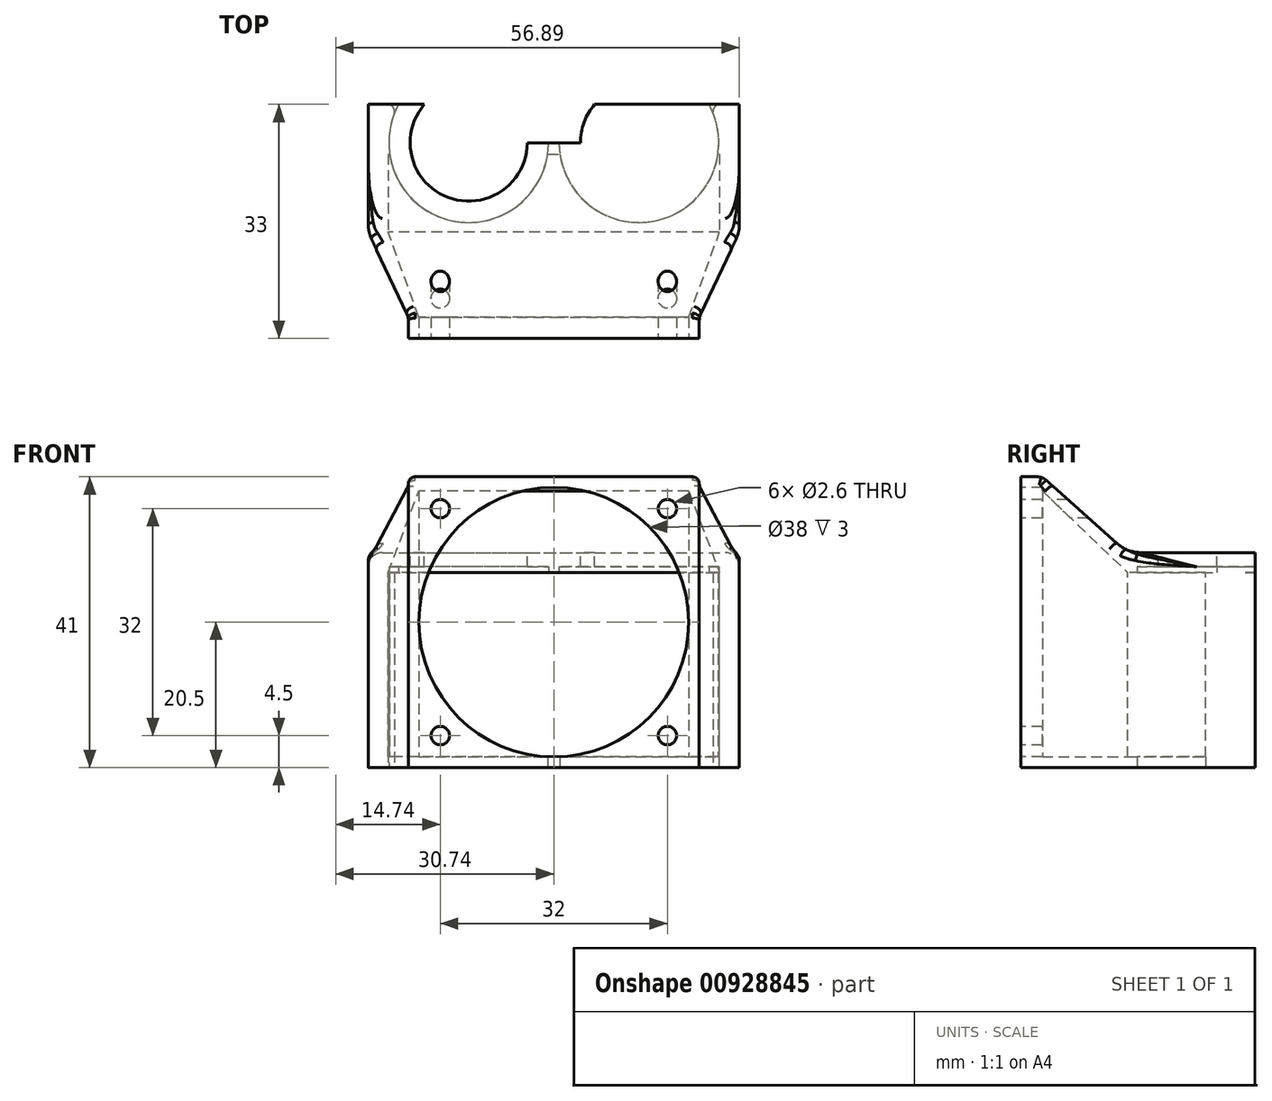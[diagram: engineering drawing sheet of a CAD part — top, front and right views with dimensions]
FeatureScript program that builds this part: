
annotation { "Feature Type Name" : "Feature", "Feature Type Description" : "" }
export const myFeature = defineFeature(function(context is Context, id is Id, definition is map)
    precondition{}
    {
        {
            var Q0;
            Q0=qCreatedBy(makeId("Front.planeOp"),FACE);
            var sketch = newSketch(context, id + "F0", { "sketchPlane" : qUnion([Q0])});
            skLineSegment(sketch, "E0.bottom", {"start": v(23.35, -13.75) * mm, "end": v(-23.35, -13.75) * mm});
            skLineSegment(sketch, "E0.top", {"start": v(23.35, 13.75) * mm, "end": v(-23.35, 13.75) * mm});
            skLineSegment(sketch, "E0.left", {"start": v(23.35, -13.75) * mm, "end": v(23.35, 13.75) * mm});
            skLineSegment(sketch, "E0.right", {"start": v(-23.35, -13.75) * mm, "end": v(-23.35, 13.75) * mm});
            skPoint(sketch, "E0.middle", {"position": v(0, 0) * mm});
            skLineSegment(sketch, "E1.bottom", {"start": v(-26.15, 16.55) * mm, "end": v(26.15, 16.55) * mm});
            skLineSegment(sketch, "E1.top", {"start": v(-26.15, -13.75) * mm, "end": v(26.15, -13.75) * mm});
            skLineSegment(sketch, "E1.left", {"start": v(-26.15, 16.55) * mm, "end": v(-26.15, -13.75) * mm});
            skLineSegment(sketch, "E1.right", {"start": v(26.15, 16.55) * mm, "end": v(26.15, -13.75) * mm});
            skLineSegment(sketch, "E2", {"start": v(-23.35, 13.75) * mm, "end": v(-26.15, 16.55) * mm});
            skLineSegment(sketch, "E3", {"start": v(23.35, 13.75) * mm, "end": v(26.15, 16.55) * mm});
            skSolve(sketch);
        }
        {
            var Q0;
            Q0=makeQuery(id+"F0.imprint","IMPRINT",FACE,{"disambiguationData":[TD([[makeQuery(id+"F0.imprint","IMPRINT",EDGE,{"derivedFrom":sQuery(id+"F0.wireOp",EDGE,"E0.top")}),-1.0]])]});
            var Q1;
            {var subQ0=sQuery(id+"F0.wireOp",EDGE,"E0.left");Q1=makeQuery(id+"F0.imprint","IMPRINT",FACE,{"disambiguationData":[TD([[makeQuery(id+"F0.imprint","IMPRINT",EDGE,{"derivedFrom":subQ0}),-1.0]])]});}
            var Q2;
            {var subQ0=sQuery(id+"F0.wireOp",EDGE,"E0.right");Q2=makeQuery(id+"F0.imprint","IMPRINT",FACE,{"disambiguationData":[TD([[makeQuery(id+"F0.imprint","IMPRINT",EDGE,{"derivedFrom":subQ0}),1.0]])]});}
            extrude(context, id + "F1", {"entities" : qUnion([Q0, Q1, Q2]), "oppositeDirection" : true, "depth" : 18 * mm, "offsetDistance" : 25 * mm});
        }
        {
            var Q0;
            Q0=makeQuery(id+"F1.opExtrude","SWEPT_FACE",FACE,{"disambiguationData":[OSD([sQuery(id+"F0.wireOp",EDGE,"E1.bottom")])]});
            var sketch = newSketch(context, id + "F2", { "sketchPlane" : qUnion([Q0])});
            skCircle(sketch, "E4", {"center": v(-12, 12.6) * mm, "radius": 8.25 * mm});
            skCircle(sketch, "E5.MirrorC", {"center": v(12, 12.6) * mm, "radius": 8.25 * mm});
            skLineSegment(sketch, "E6", {"start": v(-3.75, 12.6) * mm, "end": v(3.75, 12.6) * mm});
            skSolve(sketch);
        }
        {
            var Q0;
            Q0=makeQuery(id+"F2.imprint","IMPRINT",FACE,{"disambiguationData":[TD([[makeQuery(id+"F2.imprint","IMPRINT",EDGE,{"derivedFrom":sQuery(id+"F2.wireOp",EDGE,"E4")}),1.0]])]});
            var Q1;
            Q1=makeQuery(id+"F2.imprint","IMPRINT",FACE,{"disambiguationData":[TD([[makeQuery(id+"F2.imprint","IMPRINT",EDGE,{"derivedFrom":sQuery(id+"F2.wireOp",EDGE,"E5.MirrorC")}),-1.0]])]});
            var Q2;
            {var subQ0=sQuery(id+"F2.wireOp",EDGE,"E6");Q2=makeQuery(id+"F2.imprint","IMPRINT",FACE,{"disambiguationData":[TD([[makeQuery(id+"F2.imprint","IMPRINT",EDGE,{"derivedFrom":subQ0}),1.0]])]});}
            extrude(context, id + "F3", {"entities" : qUnion([Q0, Q1, Q2]), "operationType" : NewBodyOperationType.REMOVE, "oppositeDirection" : true, "depth" : 25 * mm, "offsetDistance" : 25 * mm});
        }
        {
            var Q0;
            Q0=qCreatedBy(makeId("Front.planeOp"),FACE);
            cPlane(context, id + "F4", {"entities" : qUnion([Q0]), "cplaneType" : CPlaneType.OFFSET, "offset" : 15 * mm, "width" : 150 * mm, "height" : 150 * mm});
        }
        {
            var Q0;
            Q0=qCreatedBy(id+"F4.planeOp",FACE);
            var sketch = newSketch(context, id + "F5", { "sketchPlane" : qUnion([Q0])});
            skLineSegment(sketch, "E7.bottom", {"start": v(-26.15, -13.75) * mm, "end": v(26.15, -13.75) * mm, "construction": true});
            skLineSegment(sketch, "E7.top", {"start": v(-26.15, 16.55) * mm, "end": v(26.15, 16.55) * mm, "construction": true});
            skLineSegment(sketch, "E7.left", {"start": v(-26.15, -13.75) * mm, "end": v(-26.15, 16.55) * mm, "construction": true});
            skLineSegment(sketch, "E7.right", {"start": v(26.15, -13.75) * mm, "end": v(26.15, 16.55) * mm, "construction": true});
            skLineSegment(sketch, "E8.bottom", {"start": v(-20.5, -13.75) * mm, "end": v(20.5, -13.75) * mm});
            skLineSegment(sketch, "E8.top", {"start": v(-20.5, 27.25) * mm, "end": v(20.5, 27.25) * mm});
            skLineSegment(sketch, "E8.left", {"start": v(-20.5, -13.75) * mm, "end": v(-20.5, 27.25) * mm});
            skLineSegment(sketch, "E8.right", {"start": v(20.5, -13.75) * mm, "end": v(20.5, 27.25) * mm});
            skPoint(sketch, "E9.centerSnap0", {"position": v(-20.5, 6.75) * mm});
            skSolve(sketch);
        }
        {
            var Q0;
            Q0=makeQuery(id+"F5.imprint","IMPRINT",FACE,{"disambiguationData":[TD([[makeQuery(id+"F5.imprint","IMPRINT",EDGE,{"derivedFrom":sQuery(id+"F5.wireOp",EDGE,"E8.bottom")}),1.0]])]});
            extrude(context, id + "F6", {"entities" : qUnion([Q0]), "oppositeDirection" : true, "depth" : 3 * mm, "offsetDistance" : 25 * mm});
        }
        {
            var Q0;
            Q0=makeQuery(id+"F6.opExtrude","CAP_FACE",FACE,{"disambiguationData":[OSD([sQuery(id+"F5.wireOp",EDGE,"E8.bottom"),sQuery(id+"F5.wireOp",EDGE,"E8.top"),sQuery(id+"F5.wireOp",EDGE,"E8.left"),sQuery(id+"F5.wireOp",EDGE,"E8.right")])],"isStart":false});
            var sketch = newSketch(context, id + "F7", { "sketchPlane" : qUnion([Q0])});
            skLineSegment(sketch, "E10.bottom", {"start": v(-19, 25.25) * mm, "end": v(19, 25.25) * mm});
            skLineSegment(sketch, "E10.top", {"start": v(-19, -13.75) * mm, "end": v(19, -13.75) * mm});
            skLineSegment(sketch, "E10.left", {"start": v(-19, 25.25) * mm, "end": v(-19, -13.75) * mm});
            skLineSegment(sketch, "E10.right", {"start": v(19, 25.25) * mm, "end": v(19, -13.75) * mm});
            skLineSegment(sketch, "E11", {"start": v(-19, 25.25) * mm, "end": v(-20.5, 27.25) * mm});
            skLineSegment(sketch, "E12", {"start": v(20.5, 27.25) * mm, "end": v(19, 25.25) * mm});
            skSolve(sketch);
        }
        {
            var Q0;
            {var subQ0=sQuery(id+"F7.wireOp",EDGE,"E10.left");Q0=makeQuery(id+"F7.imprint","IMPRINT",FACE,{"disambiguationData":[TD([[makeQuery(id+"F7.imprint","IMPRINT",EDGE,{"derivedFrom":subQ0}),-1.0]])]});}
            var Q1;
            {var subQ0=sQuery(id+"F0.wireOp",EDGE,"E0.left");Q1=makeQuery(id+"F0.imprint","IMPRINT",FACE,{"disambiguationData":[TD([[makeQuery(id+"F0.imprint","IMPRINT",EDGE,{"derivedFrom":subQ0}),-1.0]])]});}
            loft(context, id + "F8", {"operationType" : NewBodyOperationType.ADD, "sheetProfilesArray" : [{ "sheetProfileEntities" : qUnion([Q0]) }, { "sheetProfileEntities" : qUnion([Q1]) }]});
        }
        {
            var Q1;
            {var subQ0=sQuery(id+"F0.wireOp",EDGE,"E0.right");Q1=makeQuery(id+"F0.imprint","IMPRINT",FACE,{"disambiguationData":[TD([[makeQuery(id+"F0.imprint","IMPRINT",EDGE,{"derivedFrom":subQ0}),1.0]])]});}
            var Q2;
            {var subQ0=sQuery(id+"F7.wireOp",EDGE,"E10.right");Q2=makeQuery(id+"F7.imprint","IMPRINT",FACE,{"disambiguationData":[TD([[makeQuery(id+"F7.imprint","IMPRINT",EDGE,{"derivedFrom":subQ0}),1.0]])]});}
            loft(context, id + "F9", {"operationType" : NewBodyOperationType.ADD, "sheetProfilesArray" : [{ "sheetProfileEntities" : qUnion([Q1]) }, { "sheetProfileEntities" : qUnion([Q2]) }]});
        }
        {
            var Q1;
            Q1=makeQuery(id+"F7.imprint","IMPRINT",FACE,{"disambiguationData":[TD([[makeQuery(id+"F7.imprint","IMPRINT",EDGE,{"derivedFrom":sQuery(id+"F7.wireOp",EDGE,"E10.bottom")}),1.0]])]});
            var Q2;
            Q2=makeQuery(id+"F0.imprint","IMPRINT",FACE,{"disambiguationData":[TD([[makeQuery(id+"F0.imprint","IMPRINT",EDGE,{"derivedFrom":sQuery(id+"F0.wireOp",EDGE,"E0.top")}),-1.0]])]});
            loft(context, id + "F10", {"operationType" : NewBodyOperationType.ADD, "sheetProfilesArray" : [{ "sheetProfileEntities" : qUnion([Q1]) }, { "sheetProfileEntities" : qUnion([Q2]) }]});
        }
        {
            var Q0;
            Q0=makeQuery(id+"F6.opExtrude","CAP_FACE",FACE,{"disambiguationData":[OSD([sQuery(id+"F5.wireOp",EDGE,"E8.bottom"),sQuery(id+"F5.wireOp",EDGE,"E8.top"),sQuery(id+"F5.wireOp",EDGE,"E8.left"),sQuery(id+"F5.wireOp",EDGE,"E8.right")])],"isStart":true});
            var sketch = newSketch(context, id + "F11", { "sketchPlane" : qUnion([Q0])});
            skCircle(sketch, "E13", {"center": v(0, 6.75) * mm, "radius": 19 * mm});
            skLineSegment(sketch, "E14", {"start": v(-20.5, 6.75) * mm, "end": v(20.5, 6.75) * mm, "construction": true});
            skLineSegment(sketch, "E15", {"start": v(0, 27.25) * mm, "end": v(0, -13.75) * mm, "construction": true});
            skPoint(sketch, "E16", {"position": v(-16, 22.75) * mm});
            skPoint(sketch, "E17.MirrorP", {"position": v(16, 22.75) * mm});
            skPoint(sketch, "E18.MirrorP", {"position": v(-16, -9.25) * mm});
            skPoint(sketch, "E19.MirrorP", {"position": v(16, -9.25) * mm});
            skSolve(sketch);
        }
        {
            var Q0;
            Q0=sQuery(id+"F11.wireOp",VERTEX,"E16");
            var Q1;
            Q1=sQuery(id+"F11.wireOp",VERTEX,"E17.MirrorP");
            var Q2;
            Q2=sQuery(id+"F11.wireOp",VERTEX,"E19.MirrorP");
            var Q3;
            Q3=sQuery(id+"F11.wireOp",VERTEX,"E18.MirrorP");
            var Q4;
            Q4=makeQuery(id+"F1.opExtrude","SWEPT_BODY",BODY,{"disambiguationData":[OSD([sQuery(id+"F0.wireOp",EDGE,"E0.top"),sQuery(id+"F0.wireOp",EDGE,"E0.left"),sQuery(id+"F0.wireOp",EDGE,"E0.right"),sQuery(id+"F0.wireOp",EDGE,"E1.bottom"),sQuery(id+"F0.wireOp",EDGE,"E1.top"),sQuery(id+"F0.wireOp",EDGE,"E1.left"),sQuery(id+"F0.wireOp",EDGE,"E1.right")])]});
            hole(context, id + "F12", {"style" : HoleStyle.SIMPLE, "endStyle" : HoleEndStyle.BLIND, "holeDiameter" : 2.6 * mm, "majorDiameter" : 5 * mm, "holeDepth" : 10 * mm, "isTappedThrough" : true, "tappedDepth" : 12 * mm, "tapClearance" : 3, "locations" : qUnion([Q0, Q1, Q2, Q3]), "scope" : qUnion([Q4])});
        }
        {
            var Q0;
            Q0=qSketchRegion(id+"F11",true);
            var Q1;
            Q1=makeQuery(id+"F6.opExtrude","CAP_FACE",FACE,{"disambiguationData":[OSD([sQuery(id+"F5.wireOp",EDGE,"E8.bottom"),sQuery(id+"F5.wireOp",EDGE,"E8.top"),sQuery(id+"F5.wireOp",EDGE,"E8.left"),sQuery(id+"F5.wireOp",EDGE,"E8.right")])],"isStart":false});
            extrude(context, id + "F13", {"entities" : qUnion([Q0]), "operationType" : NewBodyOperationType.REMOVE, "endBound" : BoundingType.UP_TO_SURFACE, "oppositeDirection" : true, "depth" : 25 * mm, "endBoundEntityFace" : qUnion([Q1]), "offsetDistance" : 25 * mm});
        }
        {
            var Q0;
            {var subQ0=sQuery(id+"F7.wireOp",EDGE,"E10.top");var subQ1=sQuery(id+"F5.wireOp",EDGE,"E8.bottom");var subQ2=sQuery(id+"F0.wireOp",EDGE,"E1.left");var subQ3=sQuery(id+"F0.wireOp",EDGE,"E1.top");var subQ4=sQuery(id+"F0.wireOp",EDGE,"E0.right");var subQ5=sQuery(id+"F0.wireOp",EDGE,"E1.right");var subQ6=sQuery(id+"F0.wireOp",EDGE,"E0.left");Q0=makeQuery(id+"F9.boolean.opBoolean","MERGE",FACE,{"derivedFrom":[makeQuery(id+"F1.opExtrude","SWEPT_FACE",FACE,{"disambiguationData":[OSD([subQ3]),TDD([makeQuery(id+"F0.imprint","IMPRINT",EDGE,{"disambiguationData":[TD([[makeQuery(id+"F0.imprint","INTERSECT",VERTEX,{"derivedFrom":[subQ4,subQ3]}),1.0]])],"derivedFrom":subQ3})])]}),makeQuery(id+"F8.boolean.opBoolean","MERGE",FACE,{"derivedFrom":[makeQuery(id+"F1.opExtrude","SWEPT_FACE",FACE,{"disambiguationData":[OSD([subQ3]),TDD([makeQuery(id+"F0.imprint","IMPRINT",EDGE,{"disambiguationData":[TD([[makeQuery(id+"F0.imprint","INTERSECT",VERTEX,{"derivedFrom":[subQ6,subQ3]}),-1.0]])],"derivedFrom":subQ3})])]}),makeQuery(id+"F6.opExtrude","SWEPT_FACE",FACE,{"disambiguationData":[OSD([subQ1])]}),makeQuery(id+"F8.opLoft","SWEPT_FACE",FACE,{"disambiguationData":[OSD([subQ6,subQ3,subQ5,subQ1,sQuery(id+"F5.wireOp",EDGE,"E8.right"),subQ0,sQuery(id+"F7.wireOp",EDGE,"E10.left")])]})]}),makeQuery(id+"F9.opLoft","SWEPT_FACE",FACE,{"disambiguationData":[OSD([subQ4,subQ3,subQ2,subQ1,sQuery(id+"F5.wireOp",EDGE,"E8.left"),subQ0,sQuery(id+"F7.wireOp",EDGE,"E10.right")])]})]});}
            var sketch = newSketch(context, id + "F14", { "sketchPlane" : qUnion([Q0])});
            skLineSegment(sketch, "E20", {"start": v(-20.5, 15) * mm, "end": v(-20.5, 12) * mm});
            skLineSegment(sketch, "E21", {"start": v(-20.5, 12) * mm, "end": v(-26.15, 0) * mm});
            skLineSegment(sketch, "E22", {"start": v(-26.15, 0) * mm, "end": v(-26.15, -11) * mm});
            skLineSegment(sketch, "E23", {"start": v(-26.15, -11) * mm, "end": v(26.15, -11) * mm});
            skLineSegment(sketch, "E24", {"start": v(26.15, -11) * mm, "end": v(26.15, 0) * mm});
            skLineSegment(sketch, "E25", {"start": v(26.15, 0) * mm, "end": v(20.5, 12) * mm});
            skLineSegment(sketch, "E26", {"start": v(20.5, 12) * mm, "end": v(20.5, 15) * mm});
            skLineSegment(sketch, "E27", {"start": v(20.5, 15) * mm, "end": v(-20.5, 15) * mm});
            skLineSegment(sketch, "E28", {"start": v(-21.15, -17.98) * mm, "end": v(-22.65, -11) * mm});
            skLineSegment(sketch, "E29.MirrorCS", {"start": v(21.15, -17.98) * mm, "end": v(22.65, -11) * mm});
            skLineSegment(sketch, "E30", {"start": v(-21.15, -17.98) * mm, "end": v(-26.15, -18) * mm});
            skLineSegment(sketch, "E31", {"start": v(-26.15, -18) * mm, "end": v(-26.15, -11) * mm});
            skLineSegment(sketch, "E32.MirrorCS", {"start": v(21.15, -17.98) * mm, "end": v(26.15, -18) * mm});
            skLineSegment(sketch, "E33.MirrorCS", {"start": v(26.15, -18) * mm, "end": v(26.15, -11) * mm});
            skSolve(sketch);
        }
        {
            var Q0;
            Q0=makeQuery(id+"F14.imprint","IMPRINT",FACE,{"disambiguationData":[TD([[makeQuery(id+"F14.imprint","IMPRINT",EDGE,{"derivedFrom":sQuery(id+"F14.wireOp",EDGE,"E20")}),-1.0]])]});
            var Q1;
            {var subQ1=sQuery(id+"F5.wireOp",EDGE,"E8.bottom");Q1=makeQuery(id+"F14.imprint","IMPRINT",FACE,{"disambiguationData":[TD([[makeQuery(id+"F14.imprint","IMPRINT",EDGE,{"derivedFrom":makeQuery(id+"F6.opExtrude","CAP_EDGE",EDGE,{"disambiguationData":[OSD([subQ1])],"isStart":false})}),-1.0]])]});}
            extrude(context, id + "F15", {"entities" : qUnion([Q0, Q1]), "operationType" : NewBodyOperationType.ADD, "oppositeDirection" : true, "depth" : 1.5 * mm, "offsetDistance" : 25 * mm});
        }
        {
            var Q0;
            {var subQ0=sQuery(id+"F14.wireOp",EDGE,"E28");Q0=makeQuery(id+"F14.imprint","IMPRINT",FACE,{"disambiguationData":[TD([[makeQuery(id+"F14.imprint","IMPRINT",EDGE,{"derivedFrom":subQ0}),1.0]])]});}
            var Q1;
            {var subQ0=sQuery(id+"F14.wireOp",EDGE,"E29.MirrorCS");Q1=makeQuery(id+"F14.imprint","IMPRINT",FACE,{"disambiguationData":[TD([[makeQuery(id+"F14.imprint","IMPRINT",EDGE,{"derivedFrom":subQ0}),-1.0]])]});}
            var Q2;
            {var subQ0=sQuery(id+"F14.wireOp",EDGE,"E33.MirrorCS");Q2=makeQuery(id+"F14.imprint","IMPRINT",FACE,{"disambiguationData":[TD([[makeQuery(id+"F14.imprint","IMPRINT",EDGE,{"derivedFrom":subQ0}),1.0]])]});}
            var Q3;
            {var subQ0=sQuery(id+"F14.wireOp",EDGE,"E31");Q3=makeQuery(id+"F14.imprint","IMPRINT",FACE,{"disambiguationData":[TD([[makeQuery(id+"F14.imprint","IMPRINT",EDGE,{"derivedFrom":subQ0}),-1.0]])]});}
            var Q4;
            Q4=makeQuery(id+"F1.opExtrude","SWEPT_FACE",FACE,{"disambiguationData":[OSD([sQuery(id+"F0.wireOp",EDGE,"E0.top")])]});
            extrude(context, id + "F16", {"entities" : qUnion([Q0, Q1, Q2, Q3]), "operationType" : NewBodyOperationType.ADD, "endBound" : BoundingType.UP_TO_SURFACE, "oppositeDirection" : true, "depth" : 25 * mm, "endBoundEntityFace" : qUnion([Q4]), "offsetDistance" : 25 * mm});
        }
        {
            var Q0;
            Q0=makeQuery(id+"F1.opExtrude","SWEPT_FACE",FACE,{"disambiguationData":[OSD([sQuery(id+"F0.wireOp",EDGE,"E0.top")])]});
            var sketch = newSketch(context, id + "F17", { "sketchPlane" : qUnion([Q0])});
            skCircle(sketch, "E34", {"center": v(-12, -12.6) * mm, "radius": 11.25 * mm});
            skCircle(sketch, "E35.MirrorC", {"center": v(12, -12.6) * mm, "radius": 11.25 * mm});
            skSolve(sketch);
        }
        {
            var Q0;
            Q0=qSketchRegion(id+"F17",true);
            extrude(context, id + "F18", {"entities" : qUnion([Q0]), "operationType" : NewBodyOperationType.REMOVE, "oppositeDirection" : true, "depth" : .8 * mm, "offsetDistance" : 25 * mm, "hasSecondDirection" : true, "secondDirectionOppositeDirection" : false, "secondDirectionDepth" : 48.5 * mm});
        }
        {
            var Q0;
            Q0=makeQuery(id+"F18.boolean.opBoolean","INTERSECT",EDGE,{"derivedFrom":[makeQuery(id+"F16.opExtrude","SWEPT_FACE",FACE,{"disambiguationData":[OSD([sQuery(id+"F14.wireOp",EDGE,"E30")])]}),makeQuery(id+"F18.opExtrude","SWEPT_FACE",FACE,{"disambiguationData":[OSD([sQuery(id+"F17.wireOp",EDGE,"E34")])]})]});
            var Q1;
            Q1=makeQuery(id+"F18.boolean.opBoolean","INTERSECT",EDGE,{"derivedFrom":[makeQuery(id+"F16.opExtrude","SWEPT_FACE",FACE,{"disambiguationData":[OSD([sQuery(id+"F14.wireOp",EDGE,"E32.MirrorCS")])]}),makeQuery(id+"F18.opExtrude","SWEPT_FACE",FACE,{"disambiguationData":[OSD([sQuery(id+"F17.wireOp",EDGE,"E35.MirrorC")])]})]});
            fillet(context, id + "F19", {"entities" : qUnion([Q0, Q1]), "radius" : 1 * mm, "tangentPropagation" : true, "allowEdgeOverflow" : false});
        }
        {
            var Q0;
            Q0=makeQuery(id+"F1.opExtrude","SWEPT_EDGE",EDGE,{"disambiguationData":[OSD([sQuery(id+"F0.wireOp",EDGE,"E1.bottom"),sQuery(id+"F0.wireOp",EDGE,"E1.left"),sQuery(id+"F0.wireOp",EDGE,"E2")])]});
            var Q1;
            Q1=makeQuery(id+"F1.opExtrude","SWEPT_EDGE",EDGE,{"disambiguationData":[OSD([sQuery(id+"F0.wireOp",EDGE,"E1.bottom"),sQuery(id+"F0.wireOp",EDGE,"E1.right"),sQuery(id+"F0.wireOp",EDGE,"E3")])]});
            var Q2;
            {var subQ0=sQuery(id+"F5.wireOp",EDGE,"E8.top");Q2=makeQuery(id+"F10.boolean.opBoolean","MERGE",EDGE,{"derivedFrom":[makeQuery(id+"F6.opExtrude","CAP_EDGE",EDGE,{"disambiguationData":[OSD([subQ0])],"isStart":false}),makeQuery(id+"F10.opLoft","MID_CAP_EDGE",EDGE,{"disambiguationData":[OSD([subQ0,sQuery(id+"F5.wireOp",EDGE,"E8.left"),sQuery(id+"F5.wireOp",EDGE,"E8.right"),sQuery(id+"F7.wireOp",EDGE,"E11"),sQuery(id+"F7.wireOp",EDGE,"E12")])],"capPos":0.0})]});}
            var Q3;
            {var subQ0=sQuery(id+"F5.wireOp",EDGE,"E8.right");Q3=makeQuery(id+"F8.boolean.opBoolean","MERGE",EDGE,{"derivedFrom":[makeQuery(id+"F6.opExtrude","CAP_EDGE",EDGE,{"disambiguationData":[OSD([subQ0])],"isStart":false}),makeQuery(id+"F8.opLoft","MID_CAP_EDGE",EDGE,{"disambiguationData":[OSD([sQuery(id+"F5.wireOp",EDGE,"E8.bottom"),sQuery(id+"F5.wireOp",EDGE,"E8.top"),subQ0,sQuery(id+"F7.wireOp",EDGE,"E11")])],"capPos":0.0})]});}
            var Q4;
            {var subQ0=sQuery(id+"F5.wireOp",EDGE,"E8.left");Q4=makeQuery(id+"F9.boolean.opBoolean","MERGE",EDGE,{"derivedFrom":[makeQuery(id+"F6.opExtrude","CAP_EDGE",EDGE,{"disambiguationData":[OSD([subQ0])],"isStart":false}),makeQuery(id+"F9.opLoft","MID_CAP_EDGE",EDGE,{"disambiguationData":[OSD([sQuery(id+"F5.wireOp",EDGE,"E8.bottom"),sQuery(id+"F5.wireOp",EDGE,"E8.top"),subQ0,sQuery(id+"F7.wireOp",EDGE,"E12")])],"capPos":1.0})]});}
            fillet(context, id + "F20", {"entities" : qUnion([Q0, Q1, Q2, Q3, Q4]), "radius" : 2 * mm, "tangentPropagation" : true, "allowEdgeOverflow" : false});
        }
        {
            var Q0;
            {var subQ0=sQuery(id+"F0.wireOp",EDGE,"E1.bottom");Q0=makeQuery(id+"F10.boolean.opBoolean","MERGE",EDGE,{"derivedFrom":[makeQuery(id+"F1.opExtrude","CAP_EDGE",EDGE,{"disambiguationData":[OSD([subQ0])],"isStart":true}),makeQuery(id+"F10.opLoft","MID_CAP_EDGE",EDGE,{"disambiguationData":[OSD([subQ0,sQuery(id+"F0.wireOp",EDGE,"E1.left"),sQuery(id+"F0.wireOp",EDGE,"E1.right"),sQuery(id+"F0.wireOp",EDGE,"E2"),sQuery(id+"F0.wireOp",EDGE,"E3")])],"capPos":1.0})]});}
            fillet(context, id + "F21", {"entities" : qUnion([Q0]), "radius" : 5 * mm, "tangentPropagation" : true, "allowEdgeOverflow" : false});
        }
        {
            var Q0;
            {var subQ0=sQuery(id+"F0.wireOp",EDGE,"E1.left");Q0=makeQuery(id+"F9.boolean.opBoolean","MERGE",EDGE,{"derivedFrom":[makeQuery(id+"F1.opExtrude","CAP_EDGE",EDGE,{"disambiguationData":[OSD([subQ0])],"isStart":true}),makeQuery(id+"F9.opLoft","MID_CAP_EDGE",EDGE,{"disambiguationData":[OSD([sQuery(id+"F0.wireOp",EDGE,"E1.bottom"),sQuery(id+"F0.wireOp",EDGE,"E1.top"),subQ0,sQuery(id+"F0.wireOp",EDGE,"E2")])],"capPos":0.0})]});}
            var Q1;
            {var subQ0=sQuery(id+"F0.wireOp",EDGE,"E1.right");Q1=makeQuery(id+"F8.boolean.opBoolean","MERGE",EDGE,{"derivedFrom":[makeQuery(id+"F1.opExtrude","CAP_EDGE",EDGE,{"disambiguationData":[OSD([subQ0])],"isStart":true}),makeQuery(id+"F8.opLoft","MID_CAP_EDGE",EDGE,{"disambiguationData":[OSD([sQuery(id+"F0.wireOp",EDGE,"E1.bottom"),sQuery(id+"F0.wireOp",EDGE,"E1.top"),subQ0,sQuery(id+"F0.wireOp",EDGE,"E3")])],"capPos":1.0})]});}
            fillet(context, id + "F22", {"entities" : qUnion([Q0, Q1]), "radius" : 5 * mm, "tangentPropagation" : true, "allowEdgeOverflow" : false});
        }
        {
            var Q0;
            {var subQ0=sQuery(id+"F7.wireOp",EDGE,"E11");var subQ1=sQuery(id+"F5.wireOp",EDGE,"E8.right");var subQ2=sQuery(id+"F5.wireOp",EDGE,"E8.top");var subQ3=sQuery(id+"F0.wireOp",EDGE,"E3");var subQ4=sQuery(id+"F0.wireOp",EDGE,"E1.right");var subQ5=sQuery(id+"F0.wireOp",EDGE,"E1.bottom");Q0=makeQuery(id+"F10.boolean.opBoolean","MERGE",EDGE,{"derivedFrom":[makeQuery(id+"F8.opLoft","SWEPT_EDGE",EDGE,{"disambiguationData":[OSD([subQ5,subQ4,subQ3,subQ2,subQ1,subQ0])]}),makeQuery(id+"F10.opLoft","SWEPT_EDGE",EDGE,{"disambiguationData":[OSD([subQ5,subQ4,subQ3,subQ2,subQ1,subQ0])]})]});}
            var Q1;
            {var subQ0=sQuery(id+"F7.wireOp",EDGE,"E12");var subQ1=sQuery(id+"F5.wireOp",EDGE,"E8.left");var subQ2=sQuery(id+"F5.wireOp",EDGE,"E8.top");var subQ3=sQuery(id+"F0.wireOp",EDGE,"E2");var subQ4=sQuery(id+"F0.wireOp",EDGE,"E1.left");var subQ5=sQuery(id+"F0.wireOp",EDGE,"E1.bottom");Q1=makeQuery(id+"F10.boolean.opBoolean","MERGE",EDGE,{"derivedFrom":[makeQuery(id+"F9.opLoft","SWEPT_EDGE",EDGE,{"disambiguationData":[OSD([subQ5,subQ4,subQ3,subQ2,subQ1,subQ0])]}),makeQuery(id+"F10.opLoft","SWEPT_EDGE",EDGE,{"disambiguationData":[OSD([subQ5,subQ4,subQ3,subQ2,subQ1,subQ0])]})]});}
            fillet(context, id + "F23", {"entities" : qUnion([Q0, Q1]), "radius" : 1 * mm, "tangentPropagation" : true, "allowEdgeOverflow" : false});
        }
    });
